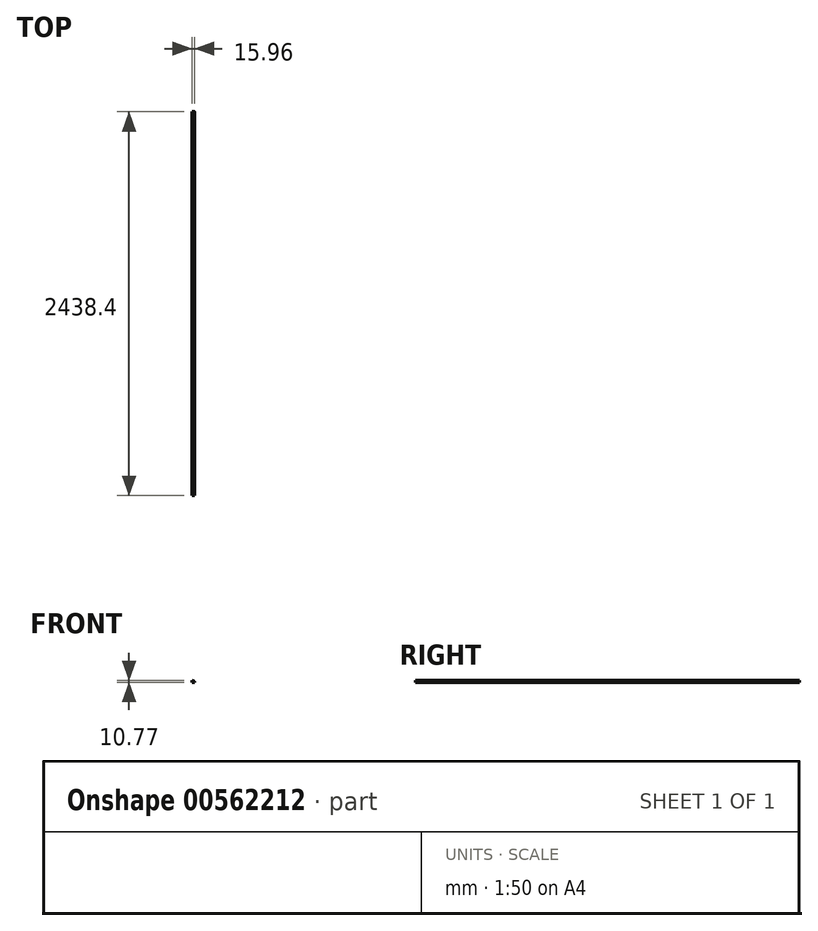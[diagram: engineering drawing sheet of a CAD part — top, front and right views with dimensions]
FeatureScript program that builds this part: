
annotation { "Feature Type Name" : "Feature", "Feature Type Description" : "" }
export const myFeature = defineFeature(function(context is Context, id is Id, definition is map)
    precondition{}
    {
        {
            var Q0;
            Q0=qCreatedBy(makeId("Front.planeOp"),FACE);
            var sketch = newSketch(context, id + "F0", { "sketchPlane" : qUnion([Q0])});
            skLineSegment(sketch, "E0.bottom", {"start": v(0, 0) * mm, "end": v(-3.14, 0) * mm});
            skLineSegment(sketch, "E0.top", {"start": v(0, 10.77) * mm, "end": v(-5.42, 10.77) * mm});
            skLineSegment(sketch, "E0.left", {"start": v(0, 0) * mm, "end": v(0, 3.07) * mm});
            skLineSegment(sketch, "E0.right", {"start": v(-15.96, 0) * mm, "end": v(-15.96, 10.77) * mm});
            skLineSegment(sketch, "E1.0", {"start": v(-5.42, 6.25) * mm, "end": v(-5.42, 8.55) * mm});
            skLineSegment(sketch, "E2.0", {"start": v(0, 10.06) * mm, "end": v(-5.42, 10.06) * mm});
            skLineSegment(sketch, "E3", {"start": v(-15.96, 10.77) * mm, "end": v(-6.93, 10.16) * mm});
            skLineSegment(sketch, "E4.0", {"start": v(-3.18, 6.25) * mm, "end": v(-5.42, 6.25) * mm});
            skPoint(sketch, "E5.newPointB", {"position": v(0, 10.77) * mm});
            skArc(sketch, "E5.filletArc", {"start": v(0, 3.07) * mm, "mid": v(-0.93, 5.32) * mm, "end": v(-3.18, 6.25) * mm});
            skPoint(sketch, "E6.visualSharp", {"position": v(-5.42, 10.06) * mm});
            skArc(sketch, "E6.filletArc", {"start": v(-5.42, 8.55) * mm, "mid": v(-5.86, 9.65) * mm, "end": v(-6.93, 10.16) * mm});
            skLineSegment(sketch, "E7", {"start": v(-3.14, 0) * mm, "end": v(-3.14, 0.5) * mm});
            skLineSegment(sketch, "E8", {"start": v(-3.14, 0.5) * mm, "end": v(-12.03, 0.5) * mm});
            skLineSegment(sketch, "E9", {"start": v(-12.03, 0.5) * mm, "end": v(-12.03, 0) * mm});
            skLineSegment(sketch, "E10.trimOffspring", {"start": v(-12.03, 0) * mm, "end": v(-15.96, 0) * mm});
            skSolve(sketch);
        }
        {
            var Q0;
            Q0=makeQuery(id+"F0.imprint","IMPRINT",FACE,{"disambiguationData":[TD([[makeQuery(id+"F0.imprint","IMPRINT",EDGE,{"derivedFrom":sQuery(id+"F0.wireOp",EDGE,"E0.bottom")}),-1.0]])]});
            extrude(context, id + "F1", {"entities" : qUnion([Q0]), "depth" : 2438.4 * mm, "offsetDistance" : 25.4 * mm});
        }
    });
